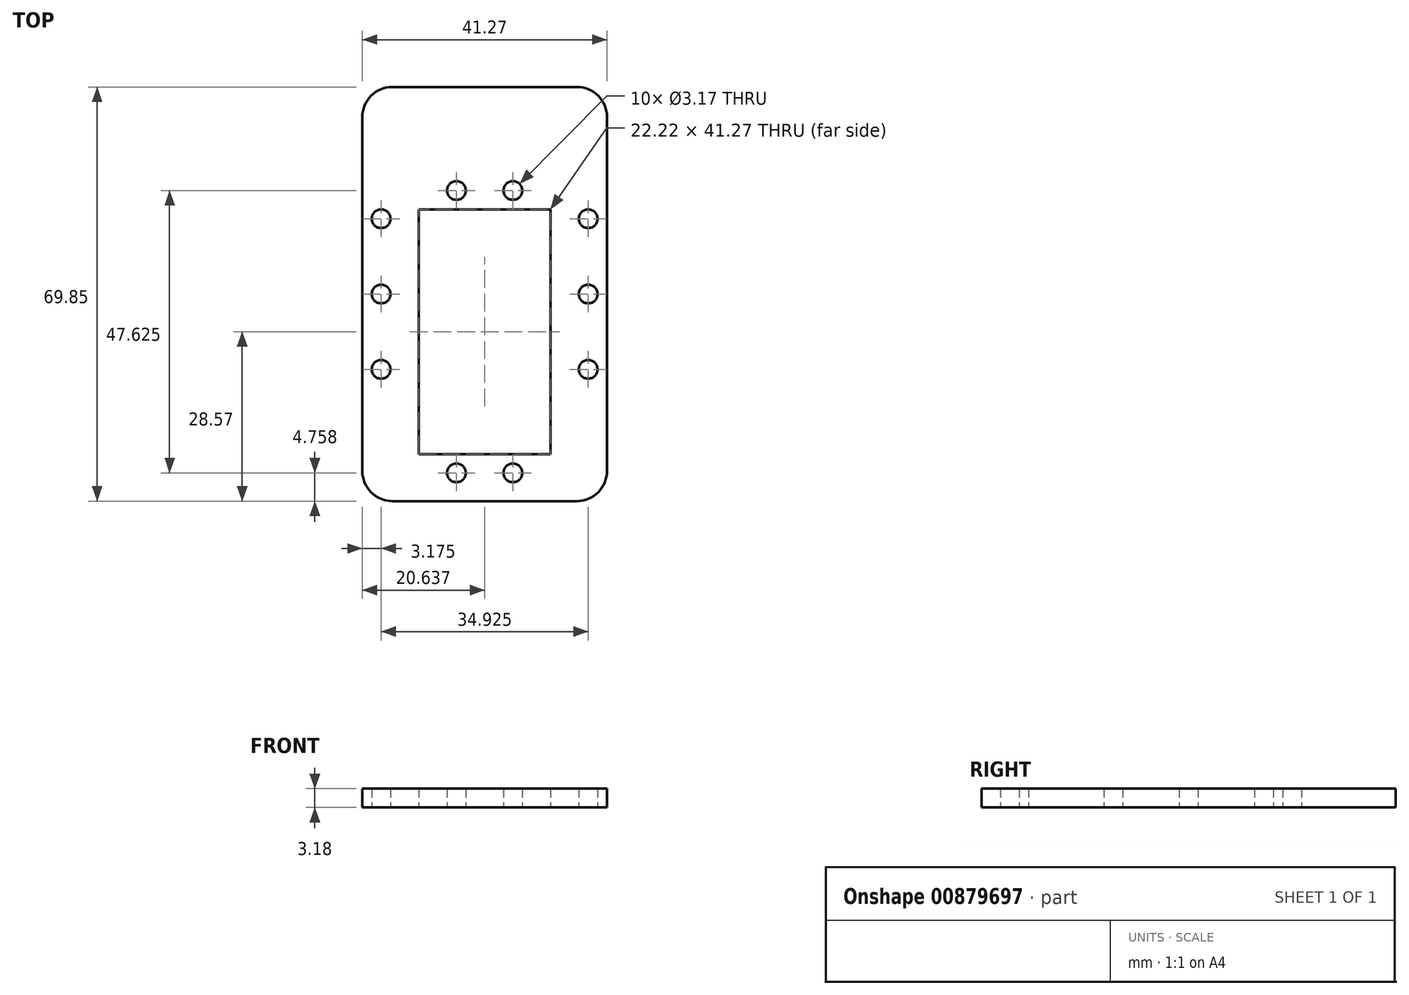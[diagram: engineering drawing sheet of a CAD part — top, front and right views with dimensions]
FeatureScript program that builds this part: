
annotation { "Feature Type Name" : "Feature", "Feature Type Description" : "" }
export const myFeature = defineFeature(function(context is Context, id is Id, definition is map)
    precondition{}
    {
        {
            var Q0;
            Q0=qCreatedBy(makeId("Top.planeOp"),FACE);
            var sketch = newSketch(context, id + "F0", { "sketchPlane" : qUnion([Q0])});
            skLineSegment(sketch, "E0.bottom", {"start": v(-53.82, 57.3) * mm, "end": v(-31.6, 57.3) * mm});
            skLineSegment(sketch, "E0.top", {"start": v(-53.82, 16.02) * mm, "end": v(-31.6, 16.02) * mm});
            skLineSegment(sketch, "E0.left", {"start": v(-53.82, 57.3) * mm, "end": v(-53.82, 16.02) * mm});
            skLineSegment(sketch, "E0.right", {"start": v(-31.6, 57.3) * mm, "end": v(-31.6, 16.02) * mm});
            skPoint(sketch, "E1", {"position": v(-42.7, 36.66) * mm});
            skPoint(sketch, "E1.positionSnap0", {"position": v(-31.6, 36.66) * mm});
            skPoint(sketch, "E1.positionSnap1", {"position": v(-42.7, 57.3) * mm});
            skLineSegment(sketch, "E2.bottom", {"start": v(-22.07, 77.94) * mm, "end": v(-63.34, 77.94) * mm});
            skLineSegment(sketch, "E2.top", {"start": v(-22.07, 8.09) * mm, "end": v(-63.34, 8.09) * mm});
            skLineSegment(sketch, "E2.left", {"start": v(-22.07, 77.94) * mm, "end": v(-22.07, 8.09) * mm});
            skLineSegment(sketch, "E2.right", {"start": v(-63.34, 77.94) * mm, "end": v(-63.34, 8.09) * mm});
            skPoint(sketch, "E2.middle", {"position": v(-42.7, 43.01) * mm});
            skCircle(sketch, "E3", {"center": v(-60.17, 55.71) * mm, "radius": 1.59 * mm});
            skCircle(sketch, "E4", {"center": v(-60.17, 43.01) * mm, "radius": 1.59 * mm});
            skCircle(sketch, "E5", {"center": v(-60.17, 30.31) * mm, "radius": 1.59 * mm});
            skCircle(sketch, "E6", {"center": v(-25.24, 30.31) * mm, "radius": 1.59 * mm});
            skCircle(sketch, "E7", {"center": v(-25.24, 43.01) * mm, "radius": 1.59 * mm});
            skCircle(sketch, "E8", {"center": v(-25.24, 55.71) * mm, "radius": 1.59 * mm});
            skCircle(sketch, "E9", {"center": v(-47.47, 60.47) * mm, "radius": 1.59 * mm});
            skCircle(sketch, "E10", {"center": v(-37.94, 60.47) * mm, "radius": 1.59 * mm});
            skCircle(sketch, "E11", {"center": v(-47.47, 12.85) * mm, "radius": 1.59 * mm});
            skCircle(sketch, "E12", {"center": v(-37.94, 12.85) * mm, "radius": 1.59 * mm});
            skSolve(sketch);
        }
        {
            var Q0;
            Q0 = qSketchRegion(id + "F0", true);
            extrude(context, id + "F1", {"entities" : qUnion([Q0]), "depth" : 3.17 * mm, "offsetDistance" : 25.4 * mm});
        }
        {
            var Q0;
            Q0=makeQuery(id+"F1.opExtrude","SWEPT_EDGE",EDGE,{"disambiguationData":[OSD([sQuery(id+"F0.wireOp",EDGE,"E2.bottom"),sQuery(id+"F0.wireOp",EDGE,"E2.left")])]});
            var Q1;
            Q1=makeQuery(id+"F1.opExtrude","SWEPT_EDGE",EDGE,{"disambiguationData":[OSD([sQuery(id+"F0.wireOp",EDGE,"E2.bottom"),sQuery(id+"F0.wireOp",EDGE,"E2.right")])]});
            var Q2;
            Q2=makeQuery(id+"F1.opExtrude","SWEPT_EDGE",EDGE,{"disambiguationData":[OSD([sQuery(id+"F0.wireOp",EDGE,"E2.top"),sQuery(id+"F0.wireOp",EDGE,"E2.right")])]});
            var Q3;
            Q3=makeQuery(id+"F1.opExtrude","SWEPT_EDGE",EDGE,{"disambiguationData":[OSD([sQuery(id+"F0.wireOp",EDGE,"E2.top"),sQuery(id+"F0.wireOp",EDGE,"E2.left")])]});
            fillet(context, id + "F2", {"entities" : qUnion([Q0, Q1, Q2, Q3]), "radius" : 5.08 * mm, "tangentPropagation" : true, "allowEdgeOverflow" : false});
        }
    });
